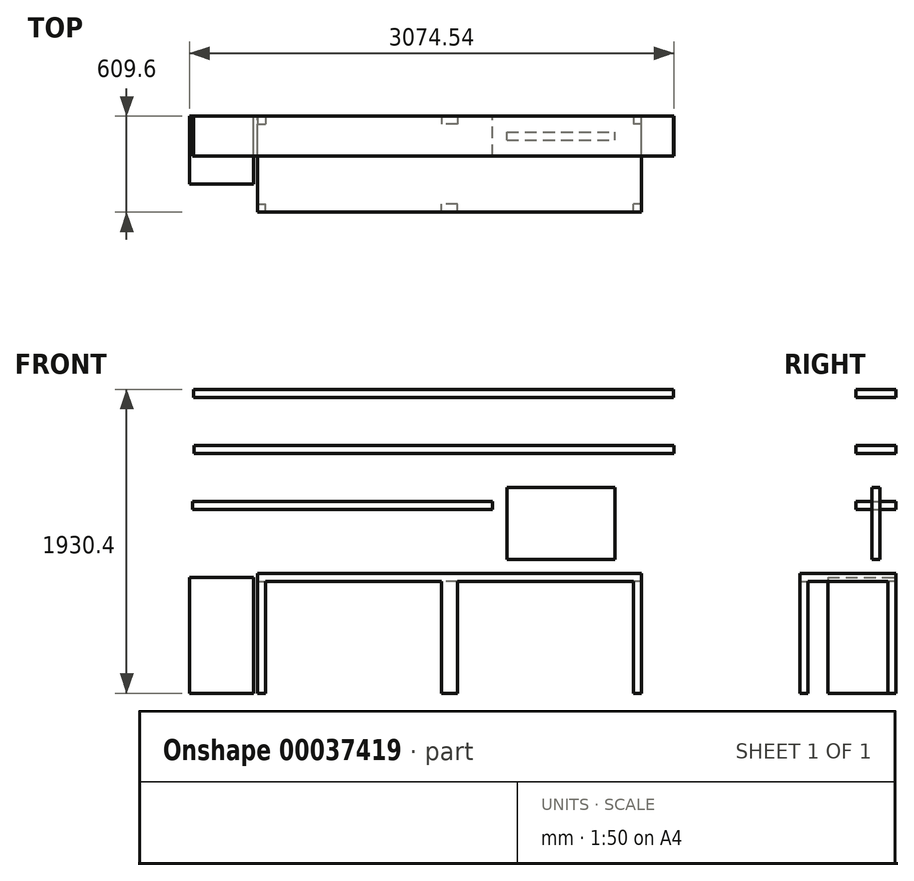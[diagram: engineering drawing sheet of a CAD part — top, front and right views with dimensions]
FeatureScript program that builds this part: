
annotation { "Feature Type Name" : "Feature", "Feature Type Description" : "" }
export const myFeature = defineFeature(function(context is Context, id is Id, definition is map)
    precondition{}
    {
        {
            var Q0;
            Q0=qCreatedBy(makeId("Front.planeOp"),FACE);
            var sketch = newSketch(context, id + "F0", { "sketchPlane" : qUnion([Q0])});
            skLineSegment(sketch, "E0.bottom", {"start": v(-1117.6, 762) * mm, "end": v(101.6, 762) * mm});
            skLineSegment(sketch, "E0.top", {"start": v(-1117.6, 711.2) * mm, "end": v(101.6, 711.2) * mm});
            skLineSegment(sketch, "E0.left", {"start": v(-1117.6, 762) * mm, "end": v(-1117.6, 711.2) * mm});
            skLineSegment(sketch, "E0.right", {"start": v(101.6, 762) * mm, "end": v(101.6, 711.2) * mm});
            skLineSegment(sketch, "E1.bottom", {"start": v(101.6, 762) * mm, "end": v(1320.8, 762) * mm});
            skLineSegment(sketch, "E1.top", {"start": v(101.6, 711.2) * mm, "end": v(1320.8, 711.2) * mm});
            skLineSegment(sketch, "E1.right", {"start": v(1320.8, 762) * mm, "end": v(1320.8, 711.2) * mm});
            skLineSegment(sketch, "E2.bottom", {"start": v(-1531.22, 1219.2) * mm, "end": v(373.78, 1219.2) * mm});
            skLineSegment(sketch, "E2.top", {"start": v(-1531.22, 1168.4) * mm, "end": v(373.78, 1168.4) * mm});
            skLineSegment(sketch, "E2.left", {"start": v(-1531.22, 1219.2) * mm, "end": v(-1531.22, 1168.4) * mm});
            skLineSegment(sketch, "E2.right", {"start": v(373.78, 1219.2) * mm, "end": v(373.78, 1168.4) * mm});
            skLineSegment(sketch, "E3.bottom", {"start": v(-1522.86, 1574.8) * mm, "end": v(1525.14, 1574.8) * mm});
            skLineSegment(sketch, "E3.top", {"start": v(-1522.86, 1524) * mm, "end": v(1525.14, 1524) * mm});
            skLineSegment(sketch, "E3.left", {"start": v(-1522.86, 1574.8) * mm, "end": v(-1522.86, 1524) * mm});
            skLineSegment(sketch, "E3.right", {"start": v(1525.14, 1574.8) * mm, "end": v(1525.14, 1524) * mm});
            skLineSegment(sketch, "E4.bottom", {"start": v(-1523.76, 1930.4) * mm, "end": v(1524.24, 1930.4) * mm});
            skLineSegment(sketch, "E4.top", {"start": v(-1523.76, 1879.6) * mm, "end": v(1524.24, 1879.6) * mm});
            skLineSegment(sketch, "E4.left", {"start": v(-1523.76, 1930.4) * mm, "end": v(-1523.76, 1879.6) * mm});
            skLineSegment(sketch, "E4.right", {"start": v(1524.24, 1930.4) * mm, "end": v(1524.24, 1879.6) * mm});
            skLineSegment(sketch, "E5.bottom", {"start": v(464.34, 1308.1) * mm, "end": v(1150.14, 1308.1) * mm});
            skLineSegment(sketch, "E5.top", {"start": v(464.34, 850.9) * mm, "end": v(1150.14, 850.9) * mm});
            skLineSegment(sketch, "E5.left", {"start": v(464.34, 1308.1) * mm, "end": v(464.34, 850.9) * mm});
            skLineSegment(sketch, "E5.right", {"start": v(1150.14, 1308.1) * mm, "end": v(1150.14, 850.9) * mm});
            skLineSegment(sketch, "E6.bottom", {"start": v(-1549.4, 0) * mm, "end": v(1549.4, 0) * mm, "construction": true});
            skLineSegment(sketch, "E6.top", {"start": v(-1549.4, 2241.55) * mm, "end": v(1549.4, 2241.55) * mm, "construction": true});
            skLineSegment(sketch, "E6.left", {"start": v(-1549.4, 0) * mm, "end": v(-1549.4, 2241.55) * mm, "construction": true});
            skLineSegment(sketch, "E6.right", {"start": v(1549.4, 0) * mm, "end": v(1549.4, 2241.55) * mm, "construction": true});
            skLineSegment(sketch, "E7.bottom", {"start": v(-1549.4, 736.6) * mm, "end": v(-1143, 736.6) * mm});
            skLineSegment(sketch, "E7.top", {"start": v(-1549.4, 0) * mm, "end": v(-1143, 0) * mm});
            skLineSegment(sketch, "E7.left", {"start": v(-1549.4, 736.6) * mm, "end": v(-1549.4, 0) * mm});
            skLineSegment(sketch, "E7.right", {"start": v(-1143, 736.6) * mm, "end": v(-1143, 0) * mm});
            skSolve(sketch);
        }
        {
            var Q0;
            Q0=makeQuery(id+"F0.imprint","IMPRINT",FACE,{"disambiguationData":[TD([[makeQuery(id+"F0.imprint","IMPRINT",EDGE,{"derivedFrom":sQuery(id+"F0.wireOp",EDGE,"E4.bottom")}),-1.0]])]});
            var Q1;
            Q1=makeQuery(id+"F0.imprint","IMPRINT",FACE,{"disambiguationData":[TD([[makeQuery(id+"F0.imprint","IMPRINT",EDGE,{"derivedFrom":sQuery(id+"F0.wireOp",EDGE,"E3.bottom")}),-1.0]])]});
            var Q2;
            Q2=makeQuery(id+"F0.imprint","IMPRINT",FACE,{"disambiguationData":[TD([[makeQuery(id+"F0.imprint","IMPRINT",EDGE,{"derivedFrom":sQuery(id+"F0.wireOp",EDGE,"E2.bottom")}),-1.0]])]});
            extrude(context, id + "F1", {"entities" : qUnion([Q0, Q1, Q2]), "depth" : 254 * mm});
        }
        {
            var Q0;
            Q0=makeQuery(id+"F0.imprint","IMPRINT",FACE,{"disambiguationData":[TD([[makeQuery(id+"F0.imprint","IMPRINT",EDGE,{"derivedFrom":sQuery(id+"F0.wireOp",EDGE,"E0.bottom")}),-1.0]])]});
            extrude(context, id + "F2", {"entities" : qUnion([Q0]), "depth" : 609.6 * mm});
        }
        {
            var Q0;
            Q0=makeQuery(id+"F0.imprint","IMPRINT",FACE,{"disambiguationData":[TD([[makeQuery(id+"F0.imprint","IMPRINT",EDGE,{"derivedFrom":sQuery(id+"F0.wireOp",EDGE,"E5.bottom")}),-1.0]])]});
            extrude(context, id + "F3", {"entities" : qUnion([Q0]), "depth" : 152.4 * mm, "hasSecondDirection" : true, "secondDirectionOppositeDirection" : false, "secondDirectionDepth" : 101.6 * mm});
        }
        {
            var Q0;
            Q0=makeQuery(id+"F0.imprint","IMPRINT",FACE,{"disambiguationData":[TD([[makeQuery(id+"F0.imprint","IMPRINT",EDGE,{"derivedFrom":sQuery(id+"F0.wireOp",EDGE,"E1.bottom")}),-1.0]])]});
            extrude(context, id + "F4", {"entities" : qUnion([Q0]), "depth" : 609.6 * mm});
        }
        {
            var Q0;
            Q0=makeQuery(id+"F4.opExtrude","SWEPT_FACE",FACE,{"disambiguationData":[OSD([sQuery(id+"F0.wireOp",EDGE,"E1.top")])]});
            var sketch = newSketch(context, id + "F5", { "sketchPlane" : qUnion([Q0])});
            skLineSegment(sketch, "E8.bottom", {"start": v(1320.8, 0) * mm, "end": v(1270, 0) * mm});
            skLineSegment(sketch, "E8.top", {"start": v(1320.8, 50.8) * mm, "end": v(1270, 50.8) * mm});
            skLineSegment(sketch, "E8.left", {"start": v(1320.8, 0) * mm, "end": v(1320.8, 50.8) * mm});
            skLineSegment(sketch, "E8.right", {"start": v(1270, 0) * mm, "end": v(1270, 50.8) * mm});
            skLineSegment(sketch, "E9.bottom", {"start": v(1320.8, 609.6) * mm, "end": v(1270, 609.6) * mm});
            skLineSegment(sketch, "E9.top", {"start": v(1320.8, 558.8) * mm, "end": v(1270, 558.8) * mm});
            skLineSegment(sketch, "E9.left", {"start": v(1320.8, 609.6) * mm, "end": v(1320.8, 558.8) * mm});
            skLineSegment(sketch, "E9.right", {"start": v(1270, 609.6) * mm, "end": v(1270, 558.8) * mm});
            skLineSegment(sketch, "E10.bottom", {"start": v(101.6, 609.6) * mm, "end": v(152.4, 609.6) * mm});
            skLineSegment(sketch, "E10.top", {"start": v(101.6, 558.8) * mm, "end": v(152.4, 558.8) * mm});
            skLineSegment(sketch, "E10.left", {"start": v(101.6, 609.6) * mm, "end": v(101.6, 558.8) * mm});
            skLineSegment(sketch, "E10.right", {"start": v(152.4, 609.6) * mm, "end": v(152.4, 558.8) * mm});
            skLineSegment(sketch, "E11.bottom", {"start": v(101.6, 0) * mm, "end": v(152.4, 0) * mm});
            skLineSegment(sketch, "E11.top", {"start": v(101.6, 50.8) * mm, "end": v(152.4, 50.8) * mm});
            skLineSegment(sketch, "E11.left", {"start": v(101.6, 0) * mm, "end": v(101.6, 50.8) * mm});
            skLineSegment(sketch, "E11.right", {"start": v(152.4, 0) * mm, "end": v(152.4, 50.8) * mm});
            skLineSegment(sketch, "E12.0", {"start": v(-1117.6, 609.6) * mm, "end": v(-1117.6, 0) * mm, "construction": true});
            skLineSegment(sketch, "E13.bottom", {"start": v(-1117.6, 609.6) * mm, "end": v(-1066.8, 609.6) * mm});
            skLineSegment(sketch, "E13.top", {"start": v(-1117.6, 558.8) * mm, "end": v(-1066.8, 558.8) * mm});
            skLineSegment(sketch, "E13.left", {"start": v(-1117.6, 609.6) * mm, "end": v(-1117.6, 558.8) * mm});
            skLineSegment(sketch, "E13.right", {"start": v(-1066.8, 609.6) * mm, "end": v(-1066.8, 558.8) * mm});
            skLineSegment(sketch, "E14.bottom", {"start": v(-1117.6, 0) * mm, "end": v(-1066.8, 0) * mm});
            skLineSegment(sketch, "E14.top", {"start": v(-1117.6, 50.8) * mm, "end": v(-1066.8, 50.8) * mm});
            skLineSegment(sketch, "E14.left", {"start": v(-1117.6, 0) * mm, "end": v(-1117.6, 50.8) * mm});
            skLineSegment(sketch, "E14.right", {"start": v(-1066.8, 0) * mm, "end": v(-1066.8, 50.8) * mm});
            skLineSegment(sketch, "E15.bottom", {"start": v(101.6, 0) * mm, "end": v(50.8, 0) * mm});
            skLineSegment(sketch, "E15.top", {"start": v(101.6, 50.8) * mm, "end": v(50.8, 50.8) * mm});
            skLineSegment(sketch, "E15.right", {"start": v(50.8, 0) * mm, "end": v(50.8, 50.8) * mm});
            skLineSegment(sketch, "E16.bottom", {"start": v(101.6, 609.6) * mm, "end": v(50.8, 609.6) * mm});
            skLineSegment(sketch, "E16.top", {"start": v(101.6, 558.8) * mm, "end": v(50.8, 558.8) * mm});
            skLineSegment(sketch, "E16.right", {"start": v(50.8, 609.6) * mm, "end": v(50.8, 558.8) * mm});
            skSolve(sketch);
        }
        {
            var Q0;
            Q0=makeQuery(id+"F5.imprint","IMPRINT",FACE,{"disambiguationData":[TD([[makeQuery(id+"F5.imprint","IMPRINT",EDGE,{"derivedFrom":sQuery(id+"F5.wireOp",EDGE,"E16.bottom")}),1.0]])]});
            var Q1;
            Q1=makeQuery(id+"F5.imprint","IMPRINT",FACE,{"disambiguationData":[TD([[makeQuery(id+"F5.imprint","IMPRINT",EDGE,{"derivedFrom":sQuery(id+"F5.wireOp",EDGE,"E13.bottom")}),-1.0]])]});
            var Q2;
            Q2=makeQuery(id+"F5.imprint","IMPRINT",FACE,{"disambiguationData":[TD([[makeQuery(id+"F5.imprint","IMPRINT",EDGE,{"derivedFrom":sQuery(id+"F5.wireOp",EDGE,"E14.bottom")}),1.0]])]});
            var Q3;
            Q3=makeQuery(id+"F5.imprint","IMPRINT",FACE,{"disambiguationData":[TD([[makeQuery(id+"F5.imprint","IMPRINT",EDGE,{"derivedFrom":sQuery(id+"F5.wireOp",EDGE,"E15.bottom")}),-1.0]])]});
            extrude(context, id + "F6", {"entities" : qUnion([Q0, Q1, Q2, Q3]), "operationType" : NewBodyOperationType.ADD, "depth" : 711.2 * mm});
        }
        {
            var Q0;
            Q0=makeQuery(id+"F5.imprint","IMPRINT",FACE,{"disambiguationData":[TD([[makeQuery(id+"F5.imprint","IMPRINT",EDGE,{"derivedFrom":sQuery(id+"F5.wireOp",EDGE,"E10.bottom")}),-1.0]])]});
            var Q1;
            Q1=makeQuery(id+"F5.imprint","IMPRINT",FACE,{"disambiguationData":[TD([[makeQuery(id+"F5.imprint","IMPRINT",EDGE,{"derivedFrom":sQuery(id+"F5.wireOp",EDGE,"E11.bottom")}),1.0]])]});
            var Q2;
            Q2=makeQuery(id+"F5.imprint","IMPRINT",FACE,{"disambiguationData":[TD([[makeQuery(id+"F5.imprint","IMPRINT",EDGE,{"derivedFrom":sQuery(id+"F5.wireOp",EDGE,"E9.bottom")}),-1.0]])]});
            var Q3;
            Q3=makeQuery(id+"F5.imprint","IMPRINT",FACE,{"disambiguationData":[TD([[makeQuery(id+"F5.imprint","IMPRINT",EDGE,{"derivedFrom":sQuery(id+"F5.wireOp",EDGE,"E8.bottom")}),1.0]])]});
            extrude(context, id + "F7", {"entities" : qUnion([Q0, Q1, Q2, Q3]), "operationType" : NewBodyOperationType.ADD, "depth" : 711.2 * mm});
        }
        {
            var Q0;
            Q0=makeQuery(id+"F0.imprint","IMPRINT",FACE,{"disambiguationData":[TD([[makeQuery(id+"F0.imprint","IMPRINT",EDGE,{"derivedFrom":sQuery(id+"F0.wireOp",EDGE,"E7.bottom")}),-1.0]])]});
            extrude(context, id + "F8", {"entities" : qUnion([Q0]), "depth" : 431.8 * mm});
        }
    });
